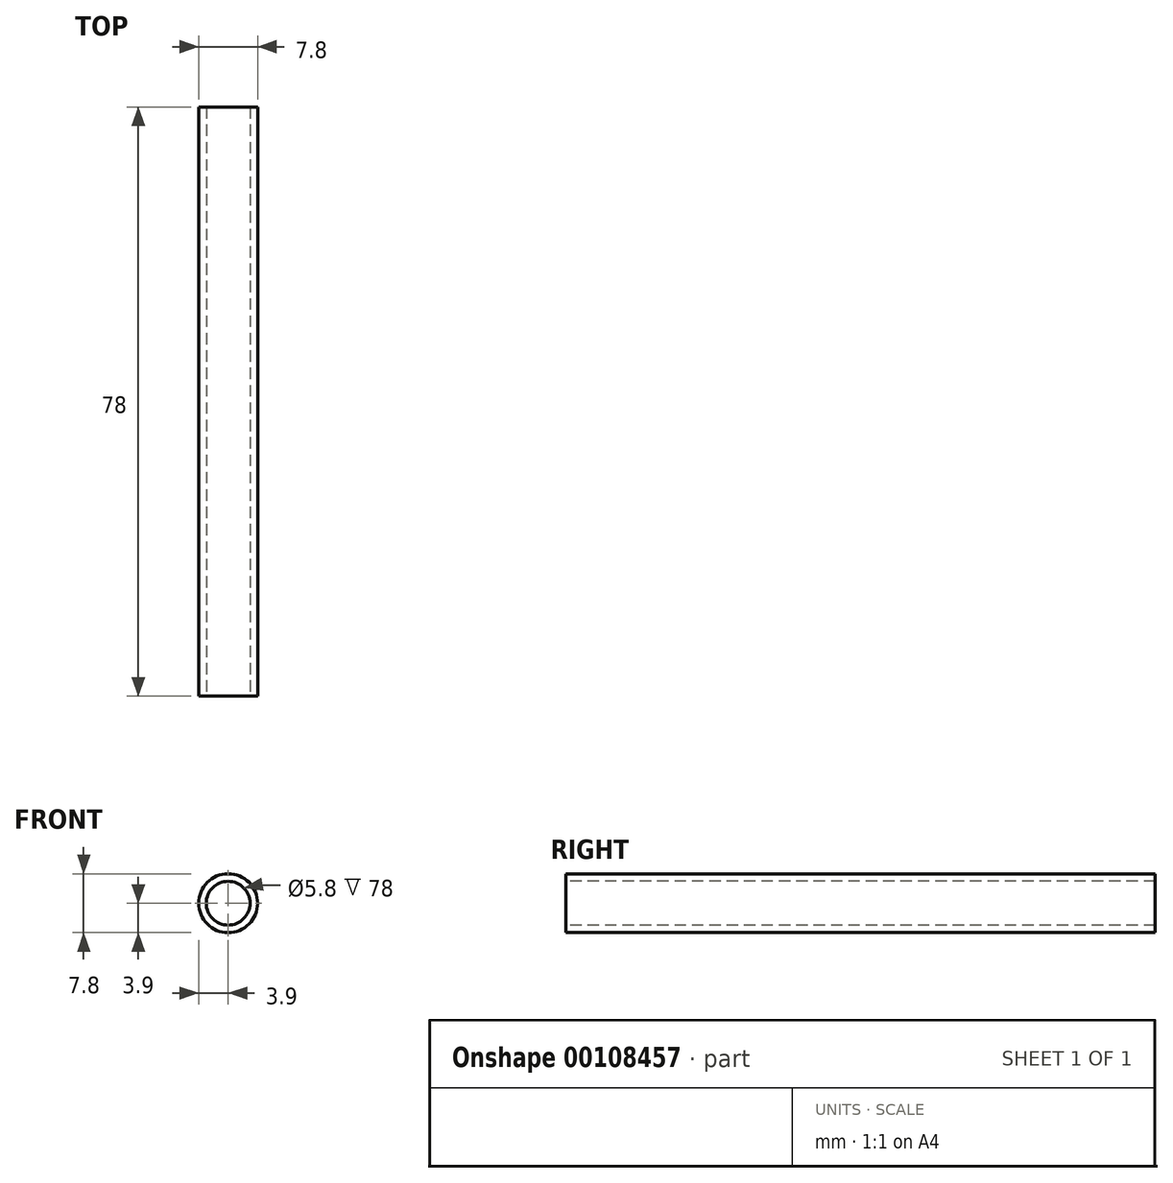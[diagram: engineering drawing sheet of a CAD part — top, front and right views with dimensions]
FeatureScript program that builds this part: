
annotation { "Feature Type Name" : "Feature", "Feature Type Description" : "" }
export const myFeature = defineFeature(function(context is Context, id is Id, definition is map)
    precondition{}
    {
        {
            var Q0;
            Q0=qCreatedBy(makeId("Top.planeOp"),FACE);
            var sketch = newSketch(context, id + "F0", { "sketchPlane" : qUnion([Q0])});
            skLineSegment(sketch, "E0", {"start": v(0, 0) * mm, "end": v(0, 78) * mm, "construction": true});
            skLineSegment(sketch, "E1.bottom", {"start": v(2.9, 0) * mm, "end": v(3.9, 0) * mm});
            skLineSegment(sketch, "E1.top", {"start": v(2.9, 78) * mm, "end": v(3.9, 78) * mm});
            skLineSegment(sketch, "E1.left", {"start": v(2.9, 0) * mm, "end": v(2.9, 78) * mm});
            skLineSegment(sketch, "E1.right", {"start": v(3.9, 0) * mm, "end": v(3.9, 78) * mm});
            skSolve(sketch);
        }
        {
            var Q0;
            Q0 = qSketchRegion(id + "F0", true);
            var Q1;
            Q1=sQuery(id+"F0.wireOp",EDGE,"E0");
            revolve(context, id + "F1", {"entities" : qUnion([Q0]), "axis" : qUnion([Q1]), "revolveType" : RevolveType.FULL});
        }
    });
